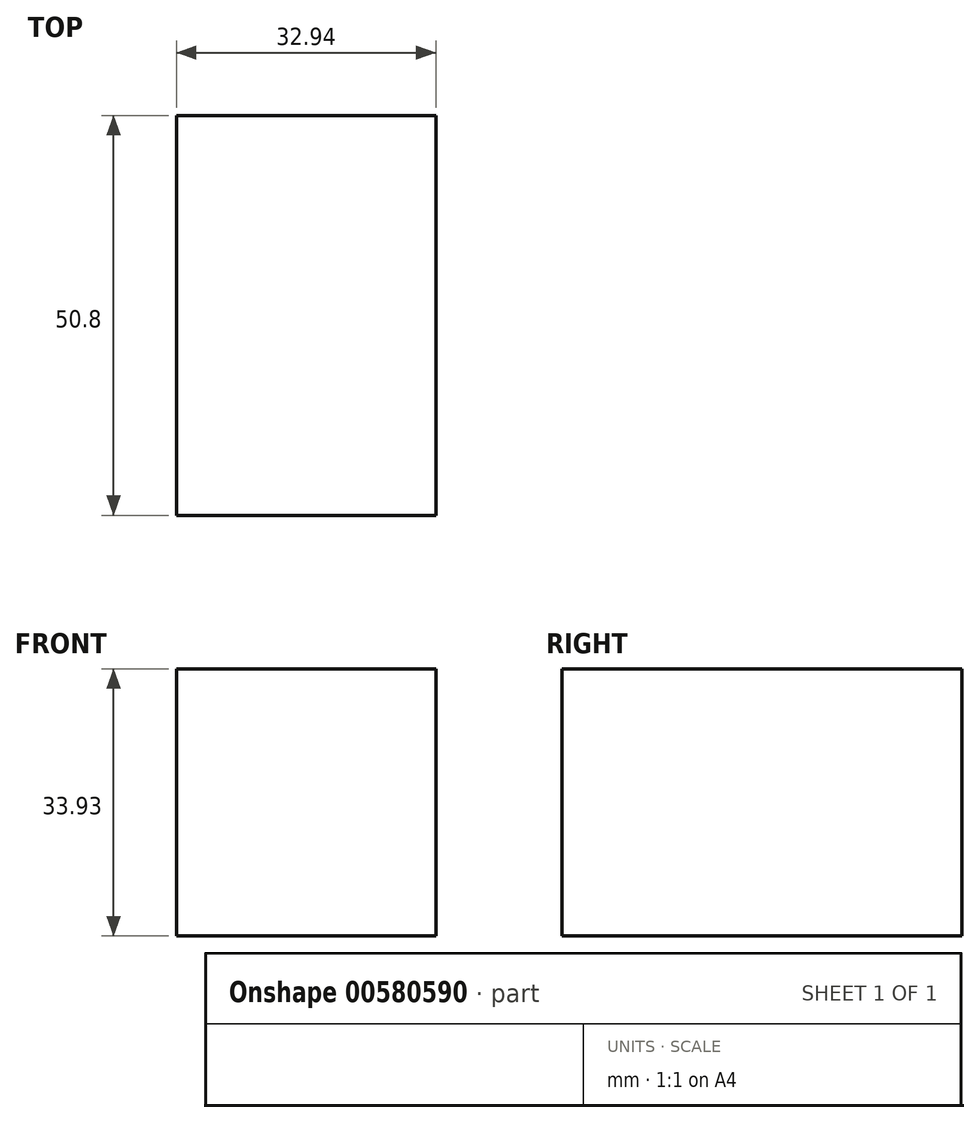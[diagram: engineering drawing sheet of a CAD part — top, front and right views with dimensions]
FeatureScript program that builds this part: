
annotation { "Feature Type Name" : "Feature", "Feature Type Description" : "" }
export const myFeature = defineFeature(function(context is Context, id is Id, definition is map)
    precondition{}
    {
        {
            var Q0;
            Q0=qCreatedBy(makeId("Front.planeOp"),FACE);
            var sketch = newSketch(context, id + "F0", { "sketchPlane" : qUnion([Q0])});
            skLineSegment(sketch, "E0", {"start": v(0, 0) * mm, "end": v(0, 33.93) * mm});
            skLineSegment(sketch, "E1", {"start": v(0, 33.93) * mm, "end": v(32.94, 33.93) * mm});
            skLineSegment(sketch, "E2", {"start": v(32.94, 33.93) * mm, "end": v(32.94, 0) * mm});
            skLineSegment(sketch, "E3", {"start": v(32.94, 0) * mm, "end": v(0, 0) * mm});
            skSolve(sketch);
        }
        {
            var Q0;
            Q0=makeQuery(id+"F0.imprint","IMPRINT",FACE,{"disambiguationData":[TD([[makeQuery(id+"F0.imprint","IMPRINT",EDGE,{"derivedFrom":sQuery(id+"F0.wireOp",EDGE,"E0")}),-1.0]])]});
            extrude(context, id + "F1", {"entities" : qUnion([Q0]), "depth" : 50.8 * mm, "offsetDistance" : 25.4 * mm});
        }
    });
